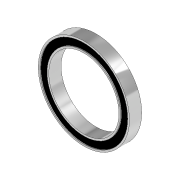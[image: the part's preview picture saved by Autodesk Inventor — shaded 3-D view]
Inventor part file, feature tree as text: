
AUTODESK INVENTOR PART (.ipt)
format: ipt  version: 2020 (Build 240168000, 168)  size: 123,904 bytes
history: native  units: in
note: dims shown in document units (in); Inventor stores cm internally (conversion verified against a paired STEP export)
features: extrude x3, sketch x3, projected_geometry x2
ambient origin geometry x8: Origin, YZ Plane, XZ Plane, XY Plane, X Axis, Y Axis, Z Axis, Center Point
bodies: Solid1 (feature_tree)
feature tree (8):
  extrude  "Extrusion1"  Depth=2.0472in
  extrude  "Extrusion2"  Depth=0.2756in
  extrude  "Extrusion3"  Depth=0.0197in TaperAngle=0.0deg
  sketch  "Sketch1"  dims[d0=1.5748in d1=2.0472in]
  sketch  "Sketch2"  dims[d2=0.2756in d3=0.0in d4=0.0394in]
  projected_geometry  "Projected Loop1"
  sketch  "Sketch3"  dims[d5=0.0394in d6=0.0197in d7=0.0in d8=0.0197in d9=0.0in]
  projected_geometry  "Projected Loop2"
